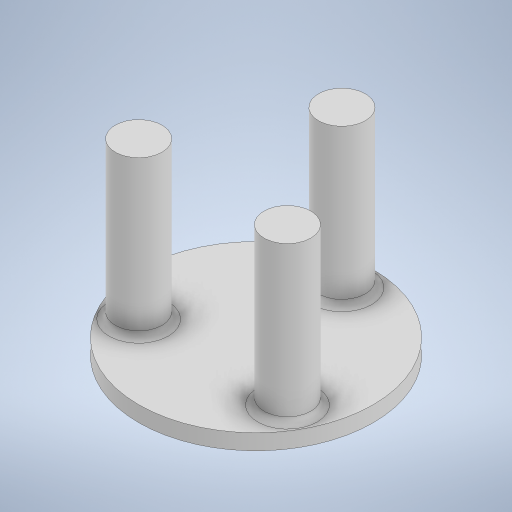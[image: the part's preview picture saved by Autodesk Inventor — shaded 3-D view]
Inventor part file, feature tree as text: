
AUTODESK INVENTOR PART (.ipt)
format: ipt  version: 2023 (Build 270158000, 158)  size: 247,808 bytes
history: native  units: mm
features: extrude x2, sketch x2, other x1, fillet x1
ambient origin geometry x8: Origin, YZ Plane, XZ Plane, XY Plane, X Axis, Y Axis, Z Axis, Center Point
bodies: Body1 (feature_tree)
feature tree (6):
  other  "ソリッド1"
  extrude  "押し出し1"  Depth=150.0mm
  extrude  "押し出し2"  Depth=10.0mm TaperAngle=0.0deg
  fillet  "フィレット1"  Radius=30.0mm
  sketch  "スケッチ1"
  sketch  "スケッチ2"
